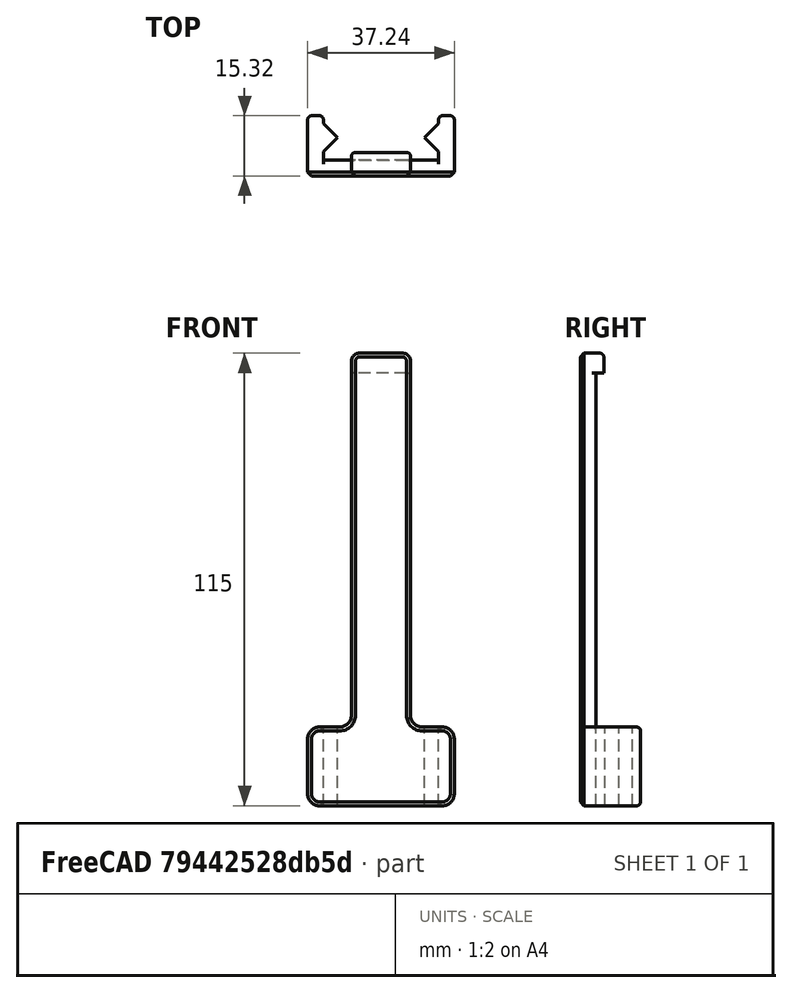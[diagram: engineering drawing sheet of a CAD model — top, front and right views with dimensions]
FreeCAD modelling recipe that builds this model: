
FCSTD DOCUMENT  (FreeCAD 0.19R)
Label: SwitchCaseSmallLatch6-22mm
License: All rights reserved
LicenseURL: http://en.wikipedia.org/wiki/All_rights_reserved
objects: PartDesign::Fillet×6, Sketcher::SketchObject×3, PartDesign::Pad×2, PartDesign::Pocket×1, PartDesign::Chamfer×1, PartDesign::Body×1, Mesh::Feature×1
note: 24 computed .brp shape members not serialized (recipe doc carries the construction recipe); baked Part::Feature solids carry a one-line shape summary decoded from their .brp

FEATURE [Sketcher::SketchObject] Sketch
  FullyConstrained = true
  MapMode = 5
  Support = -> [XY_Plane]
  sketch-geometry (14):
    g0: LineSegment StartX=-14.625 StartY=0 StartZ=0 EndX=14.625 EndY=0 EndZ=0
    g1: LineSegment StartX=14.625 StartY=0 StartZ=0 EndX=14.625 EndY=2.25 EndZ=0
    g2: LineSegment StartX=14.625 StartY=2.25 StartZ=0 EndX=11.0895 EndY=5.78553 EndZ=0
    g3: LineSegment StartX=11.0895 StartY=5.78553 StartZ=0 EndX=14.625 EndY=9.32107 EndZ=0
    g4: LineSegment StartX=14.625 StartY=9.32107 StartZ=0 EndX=14.625 EndY=11.3211 EndZ=0
    g5: LineSegment StartX=14.625 StartY=11.3211 StartZ=0 EndX=18.625 EndY=11.3211 EndZ=0
    g6: LineSegment StartX=18.625 StartY=11.3211 StartZ=0 EndX=18.625 EndY=-4 EndZ=0
    g7: LineSegment StartX=18.625 StartY=-4 StartZ=0 EndX=-18.625 EndY=-4 EndZ=0
    g8: LineSegment StartX=-18.625 StartY=-4 StartZ=0 EndX=-18.625 EndY=11.3211 EndZ=0
    g9: LineSegment StartX=-18.625 StartY=11.3211 StartZ=0 EndX=-14.625 EndY=11.3211 EndZ=0
    g10: LineSegment StartX=-14.625 StartY=11.3211 StartZ=0 EndX=-14.625 EndY=9.32107 EndZ=0
    g11: LineSegment StartX=-14.625 StartY=9.32107 StartZ=0 EndX=-11.0895 EndY=5.78553 EndZ=0
    g12: LineSegment StartX=-11.0895 StartY=5.78553 StartZ=0 EndX=-14.625 EndY=2.25 EndZ=0
    g13: LineSegment StartX=-14.625 StartY=2.25 StartZ=0 EndX=-14.625 EndY=0 EndZ=0
  constraints (41):
    c: PointOnObject(g0,g-1)
    c: PointOnObject(g0,g-1)
    c: Coincident(g0,g1)
    c: Coincident(g1,g2)
    c: Coincident(g2,g3)
    c: Coincident(g3,g4)
    c: Coincident(g4,g5)
    c: Horizontal(g5)
    c: Coincident(g5,g6)
    c: Vertical(g6)
    c: Coincident(g6,g7)
    c: Coincident(g7,g8)
    c: Coincident(g8,g9)
    c: Horizontal(g9)
    c: Coincident(g9,g10)
    c: Coincident(g10,g11)
    c: Coincident(g11,g12)
    c: Coincident(g12,g13)
    c: Coincident(g13,g0)
    c: Vertical(g8)
    c: Vertical(g13)
    c: Vertical(g10)
    c: Vertical(g1)
    c: Vertical(g4)
    c: Equal(g11,g12)
    c: Equal(g12,g3)
    c: Equal(g3,g2)
    c: Angle(g3) = 0.785398
    c: Angle(g11) = -0.785398
    c: Perpendicular(g11,g12)
    c: Perpendicular(g3,g2)
    c: Distance(g13) = 2.25
    c: Distance(g2) = 5
    c: Equal(g10,g4)
    c: Distance(g4) = 2
    c: Equal(g1,g13)
    c: Equal(g9,g5)
    c: Distance(g9) = 4
    c: Distance(g0,g7) = 4
    c: Distance(g0) = 29.25
    c: Symmetric(g6,g7,g-2)
FEATURE [PartDesign::Pad] Pad
  Direction = (1,1,1)
  Length = 115
  Length2 = 100
  Profile = -> Sketch
  Type = 0
FEATURE [Sketcher::SketchObject] Sketch001
  FullyConstrained = true
  MapMode = 5
  Placement = pos=(0,-4,0) rot=(1,0,0;1.5708rad)
  Support = -> [Pad]
  sketch-geometry (8):
    g0: LineSegment StartX=7.5 StartY=130 StartZ=0 EndX=7.5 EndY=20 EndZ=0
    g1: LineSegment StartX=7.5 StartY=20 StartZ=0 EndX=48.935 EndY=20 EndZ=0
    g2: LineSegment StartX=48.935 StartY=20 StartZ=0 EndX=48.935 EndY=139.08 EndZ=0
    g3: LineSegment StartX=48.935 StartY=139.08 StartZ=0 EndX=-48.935 EndY=139.08 EndZ=0
    g4: LineSegment StartX=-48.935 StartY=139.08 StartZ=0 EndX=-48.935 EndY=20 EndZ=0
    g5: LineSegment StartX=-48.935 StartY=20 StartZ=0 EndX=-7.5 EndY=20 EndZ=0
    g6: LineSegment StartX=-7.5 StartY=20 StartZ=0 EndX=-7.5 EndY=130 EndZ=0
    g7: LineSegment StartX=-7.5 StartY=130 StartZ=0 EndX=7.5 EndY=130 EndZ=0
  constraints (21):
    c: Vertical(g0)
    c: Coincident(g0,g1)
    c: Horizontal(g1)
    c: Coincident(g1,g2)
    c: Coincident(g2,g3)
    c: Horizontal(g3)
    c: Coincident(g3,g4)
    c: Vertical(g4)
    c: Coincident(g4,g5)
    c: Coincident(g5,g6)
    c: Coincident(g6,g7)
    c: Coincident(g7,g0)
    c: Symmetric(g0,g6,g-2)
    c: Symmetric(g0,g5,g-2)
    c: Symmetric(g1,g4,g-2)
    c: Vertical(g2)
    c: Distance(g2) = 119.08
    c: DistanceY(g0) = 20
    c: Distance(g0) = 110
    c: Distance(g3) = 97.87
    c: Distance(g7) = 15
FEATURE [PartDesign::Pocket] Pocket
  BaseFeature = -> Pad
  Length = 5
  Length2 = 100
  Profile = -> Sketch001
  Type = 1
FEATURE [Sketcher::SketchObject] Sketch002
  ExternalGeometry = -> [Pocket]
  FullyConstrained = true
  MapMode = 5
  Placement = pos=(0,0,0) rot=(0,0.707107,0.707107;3.14159rad)
  Support = -> [Pocket]
  sketch-geometry (4):
    g0: LineSegment StartX=-7.5 StartY=115 StartZ=0 EndX=-7.5 EndY=110 EndZ=0
    g1: LineSegment StartX=-7.5 StartY=110 StartZ=0 EndX=7.5 EndY=110 EndZ=0
    g2: LineSegment StartX=7.5 StartY=110 StartZ=0 EndX=7.5 EndY=115 EndZ=0
    g3: LineSegment StartX=7.5 StartY=115 StartZ=0 EndX=-7.5 EndY=115 EndZ=0
  constraints (10):
    c: Coincident(g-5,g0)
    c: PointOnObject(g0,g-5)
    c: Coincident(g0,g1)
    c: PointOnObject(g1,g-4)
    c: Horizontal(g1)
    c: Coincident(g1,g2)
    c: Coincident(g2,g-4)
    c: Coincident(g2,g3)
    c: Coincident(g3,g0)
    c: Distance(g0) = 5
FEATURE [PartDesign::Pad] Pad001
  BaseFeature = -> Pocket
  Direction = (1,1,1)
  Length = 2
  Length2 = 100
  Profile = -> Sketch002
  Type = 0
FEATURE [PartDesign::Fillet] Fillet
  Base = -> Pad001 [Edge25,Edge14,Edge16,Edge47,Edge40,Edge30]
  BaseFeature = -> Pad001
  Radius = 3
  SupportTransform = false
FEATURE [PartDesign::Fillet] Fillet001
  Base = -> Fillet [Edge45,Edge24]
  BaseFeature = -> Fillet
  Radius = 2
  SupportTransform = false
FEATURE [PartDesign::Chamfer] Chamfer
  Angle = 45
  Base = -> Fillet001 [Face2]
  BaseFeature = -> Fillet001
  ChamferType = 0
  FlipDirection = false
  Size = 1
  Size2 = 1
  SupportTransform = false
FEATURE [PartDesign::Fillet] Fillet002
  Base = -> Chamfer [Edge50]
  BaseFeature = -> Chamfer
  Radius = 1
  SupportTransform = false
FEATURE [PartDesign::Fillet] Fillet003
  Base = -> Fillet002 [Face50,Face44]
  BaseFeature = -> Fillet002
  Radius = 1
  SupportTransform = false
FEATURE [PartDesign::Fillet] Fillet004
  Base = -> Fillet003 [Edge31]
  BaseFeature = -> Fillet003
  Radius = 1
  SupportTransform = false
FEATURE [PartDesign::Fillet] Fillet005
  Base = -> Fillet004 [Edge3]
  BaseFeature = -> Fillet004
  Radius = 1
  SupportTransform = false
FEATURE [PartDesign::Body] Body
  Group = -> [Sketch,Pad,Sketch001,Pocket,Sketch002,Pad001,Fillet,Fillet001,Chamfer,Fillet002,Fillet003,Fillet004,Fillet005]
  Origin = -> Origin
  Tip = -> Fillet005
FEATURE [Mesh::Feature] Mesh  label="Fillet005 (Meshed)"
